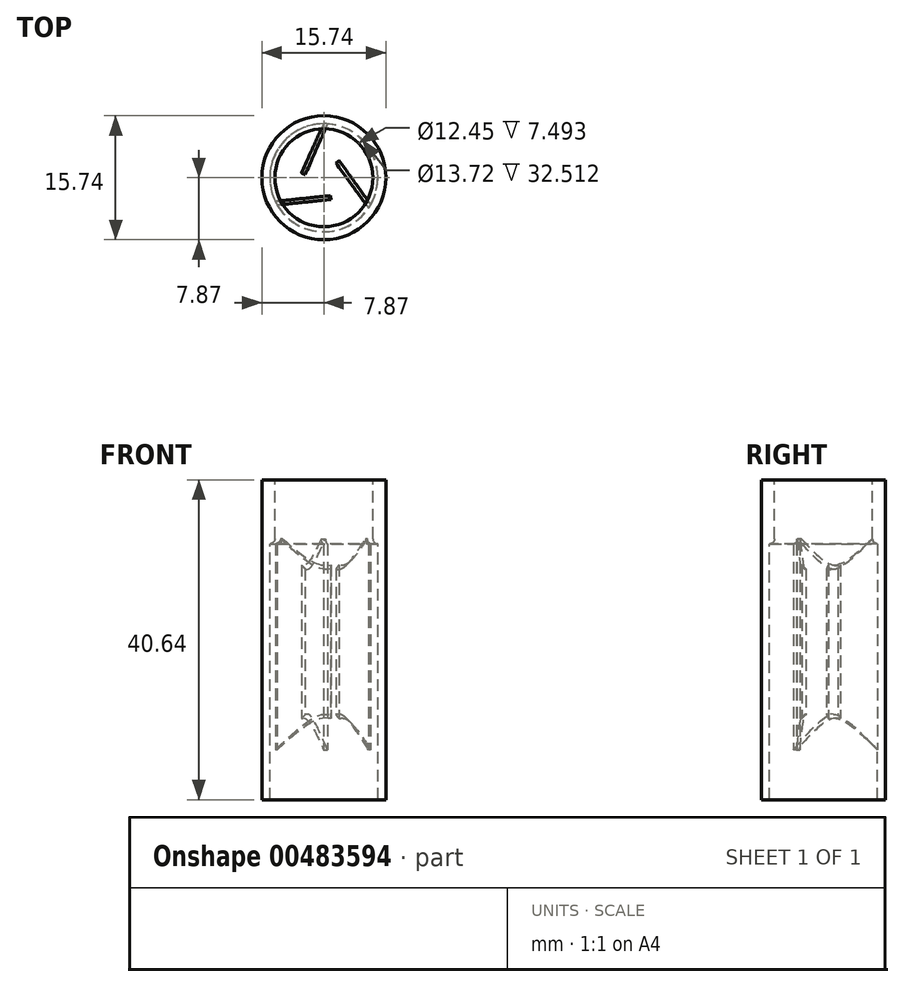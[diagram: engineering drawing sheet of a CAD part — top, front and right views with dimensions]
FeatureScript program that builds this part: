
annotation { "Feature Type Name" : "Feature", "Feature Type Description" : "" }
export const myFeature = defineFeature(function(context is Context, id is Id, definition is map)
    precondition{}
    {
        {
            var Q0;
            Q0=qCreatedBy(makeId("Front.planeOp"),FACE);
            var sketch = newSketch(context, id + "F0", { "sketchPlane" : qUnion([Q0])});
            skLineSegment(sketch, "E0", {"start": v(0, 37.35) * mm, "end": v(0, -41.74) * mm, "construction": true});
            skLineSegment(sketch, "E1", {"start": v(24.16, 0) * mm, "end": v(-24.76, 0) * mm, "construction": true});
            skLineSegment(sketch, "E2", {"start": v(7.87, 20.32) * mm, "end": v(7.87, -20.32) * mm});
            skLineSegment(sketch, "E3", {"start": v(7.87, -20.32) * mm, "end": v(6.86, -20.32) * mm});
            skLineSegment(sketch, "E4", {"start": v(6.86, -20.32) * mm, "end": v(6.86, 12.2) * mm});
            skLineSegment(sketch, "E5", {"start": v(6.86, 12.2) * mm, "end": v(6.86, 12.2) * mm});
            skLineSegment(sketch, "E6", {"start": v(6.22, 12.83) * mm, "end": v(6.22, 13.07) * mm});
            skLineSegment(sketch, "E7", {"start": v(6.22, 13.07) * mm, "end": v(6.22, 13.07) * mm});
            skLineSegment(sketch, "E8", {"start": v(6.22, 13.07) * mm, "end": v(6.22, 20.32) * mm});
            skLineSegment(sketch, "E9", {"start": v(6.22, 20.32) * mm, "end": v(7.87, 20.32) * mm});
            skPoint(sketch, "E10.visualSharp", {"position": v(6.22, 12.2) * mm});
            skArc(sketch, "E10.filletArc", {"start": v(6.22, 12.83) * mm, "mid": v(6.4, 12.38) * mm, "end": v(6.86, 12.2) * mm});
            skSolve(sketch);
        }
        {
            var Q0;
            Q0=makeQuery(id+"F0.imprint","IMPRINT",FACE,{"disambiguationData":[TD([[makeQuery(id+"F0.imprint","IMPRINT",EDGE,{"derivedFrom":sQuery(id+"F0.wireOp",EDGE,"E2")}),-1.0]])]});
            var Q1;
            Q1=sQuery(id+"F0.wireOp",EDGE,"E0");
            revolve(context, id + "F1", {"entities" : qUnion([Q0]), "axis" : qUnion([Q1]), "revolveType" : RevolveType.FULL});
        }
        {
            var Q0;
            Q0=qCreatedBy(makeId("Top.planeOp"),FACE);
            var sketch = newSketch(context, id + "F2", { "sketchPlane" : qUnion([Q0])});
            skCircle(sketch, "E11.0", {"center": v(0, 0) * mm, "radius": 6.86 * mm});
            skCircle(sketch, "E12", {"center": v(0, 0) * mm, "radius": 2.41 * mm, "construction": true});
            skLineSegment(sketch, "E13", {"start": v(0.48, 6.84) * mm, "end": v(-2.38, 0.4) * mm});
            skLineSegment(sketch, "E14", {"start": v(-2.38, 0.4) * mm, "end": v(-2.84, 0.6) * mm});
            skLineSegment(sketch, "E15", {"start": v(-2.84, 0.6) * mm, "end": v(-0.03, 6.86) * mm});
            skLineSegment(sketch, "E16.1.0", {"start": v(0.85, -2.26) * mm, "end": v(0.9, -2.77) * mm});
            skLineSegment(sketch, "E16.1.1", {"start": v(0.9, -2.77) * mm, "end": v(-5.92, -3.46) * mm});
            skLineSegment(sketch, "E16.1.2", {"start": v(-6.16, -3) * mm, "end": v(0.85, -2.26) * mm});
            skLineSegment(sketch, "E16.2.0", {"start": v(1.53, 1.86) * mm, "end": v(1.94, 2.16) * mm});
            skLineSegment(sketch, "E16.2.1", {"start": v(1.94, 2.16) * mm, "end": v(5.95, -3.4) * mm});
            skLineSegment(sketch, "E16.2.2", {"start": v(5.69, -3.83) * mm, "end": v(1.53, 1.86) * mm});
            skSolve(sketch);
        }
        {
            var Q0;
            Q0=makeQuery(id+"F2.imprint","IMPRINT",FACE,{"disambiguationData":[TD([[makeQuery(id+"F2.imprint","IMPRINT",EDGE,{"derivedFrom":sQuery(id+"F2.wireOp",EDGE,"E16.1.0")}),-1.0]])]});
            var Q1;
            Q1=makeQuery(id+"F2.imprint","IMPRINT",FACE,{"disambiguationData":[TD([[makeQuery(id+"F2.imprint","IMPRINT",EDGE,{"derivedFrom":sQuery(id+"F2.wireOp",EDGE,"E16.2.0")}),-1.0]])]});
            var Q2;
            {var subQ0=sQuery(id+"F2.wireOp",EDGE,"E13");Q2=makeQuery(id+"F2.imprint","IMPRINT",FACE,{"disambiguationData":[TD([[makeQuery(id+"F2.imprint","IMPRINT",EDGE,{"derivedFrom":subQ0}),-1.0]])]});}
            extrude(context, id + "F3", {"entities" : qUnion([Q0, Q1, Q2]), "operationType" : NewBodyOperationType.ADD, "endBound" : BoundingType.SYMMETRIC, "depth" : 38.1 * mm, "offsetDistance" : 25.4 * mm});
        }
        {
            var Q0;
            Q0=qCreatedBy(makeId("Front.planeOp"),FACE);
            var sketch = newSketch(context, id + "F4", { "sketchPlane" : qUnion([Q0])});
            skPoint(sketch, "E17.0", {"position": v(6.86, 12.2) * mm});
            skLineSegment(sketch, "E18.0", {"start": v(6.86, -20.32) * mm, "end": v(6.86, -13.97) * mm});
            skPoint(sketch, "E19", {"position": v(6.86, -13.97) * mm});
            skLineSegment(sketch, "E20", {"start": v(6.86, -13.97) * mm, "end": v(0, -7.11) * mm});
            skLineSegment(sketch, "E21", {"start": v(0, -7.11) * mm, "end": v(0, -20.32) * mm});
            skLineSegment(sketch, "E22", {"start": v(0, -20.32) * mm, "end": v(6.86, -20.32) * mm});
            skLineSegment(sketch, "E23", {"start": v(6.86, 12.2) * mm, "end": v(6.86, 12.2) * mm});
            skPoint(sketch, "E24.start.orphan", {"position": v(0, 5.33) * mm});
            skPoint(sketch, "E25.start.orphan", {"position": v(0, 12.2) * mm});
            skPoint(sketch, "E26.0", {"position": v(6.22, 12.83) * mm});
            skPoint(sketch, "E27.0", {"position": v(6.22, 13.07) * mm});
            skLineSegment(sketch, "E28", {"start": v(0, 12.83) * mm, "end": v(0, 6.6) * mm});
            skLineSegment(sketch, "E29", {"start": v(0, 6.6) * mm, "end": v(6.22, 12.83) * mm});
            skPoint(sketch, "E30.0", {"position": v(6.22, 20.32) * mm});
            skLineSegment(sketch, "E31", {"start": v(6.22, 20.32) * mm, "end": v(0, 20.32) * mm});
            skLineSegment(sketch, "E32", {"start": v(0, 20.32) * mm, "end": v(0, 12.83) * mm});
            skLineSegment(sketch, "E33", {"start": v(6.22, 20.32) * mm, "end": v(6.22, 20.32) * mm});
            skLineSegment(sketch, "E34", {"start": v(6.22, 12.83) * mm, "end": v(6.22, 20.32) * mm});
            skSolve(sketch);
        }
        {
            var Q0;
            Q0=makeQuery(id+"F4.imprint","IMPRINT",FACE,{"disambiguationData":[TD([[makeQuery(id+"F4.imprint","IMPRINT",EDGE,{"derivedFrom":sQuery(id+"F4.wireOp",EDGE,"E18.0")}),1.0]])]});
            var Q1;
            Q1=makeQuery(id+"F4.imprint","IMPRINT",FACE,{"disambiguationData":[TD([[makeQuery(id+"F4.imprint","IMPRINT",EDGE,{"derivedFrom":sQuery(id+"F4.wireOp",EDGE,"E28")}),1.0]])]});
            var Q2;
            Q2=sQuery(id+"F0.wireOp",EDGE,"E0");
            revolve(context, id + "F5", {"operationType" : NewBodyOperationType.REMOVE, "entities" : qUnion([Q0, Q1]), "axis" : qUnion([Q2]), "revolveType" : RevolveType.FULL, "oppositeDirection" : true});
        }
    });
